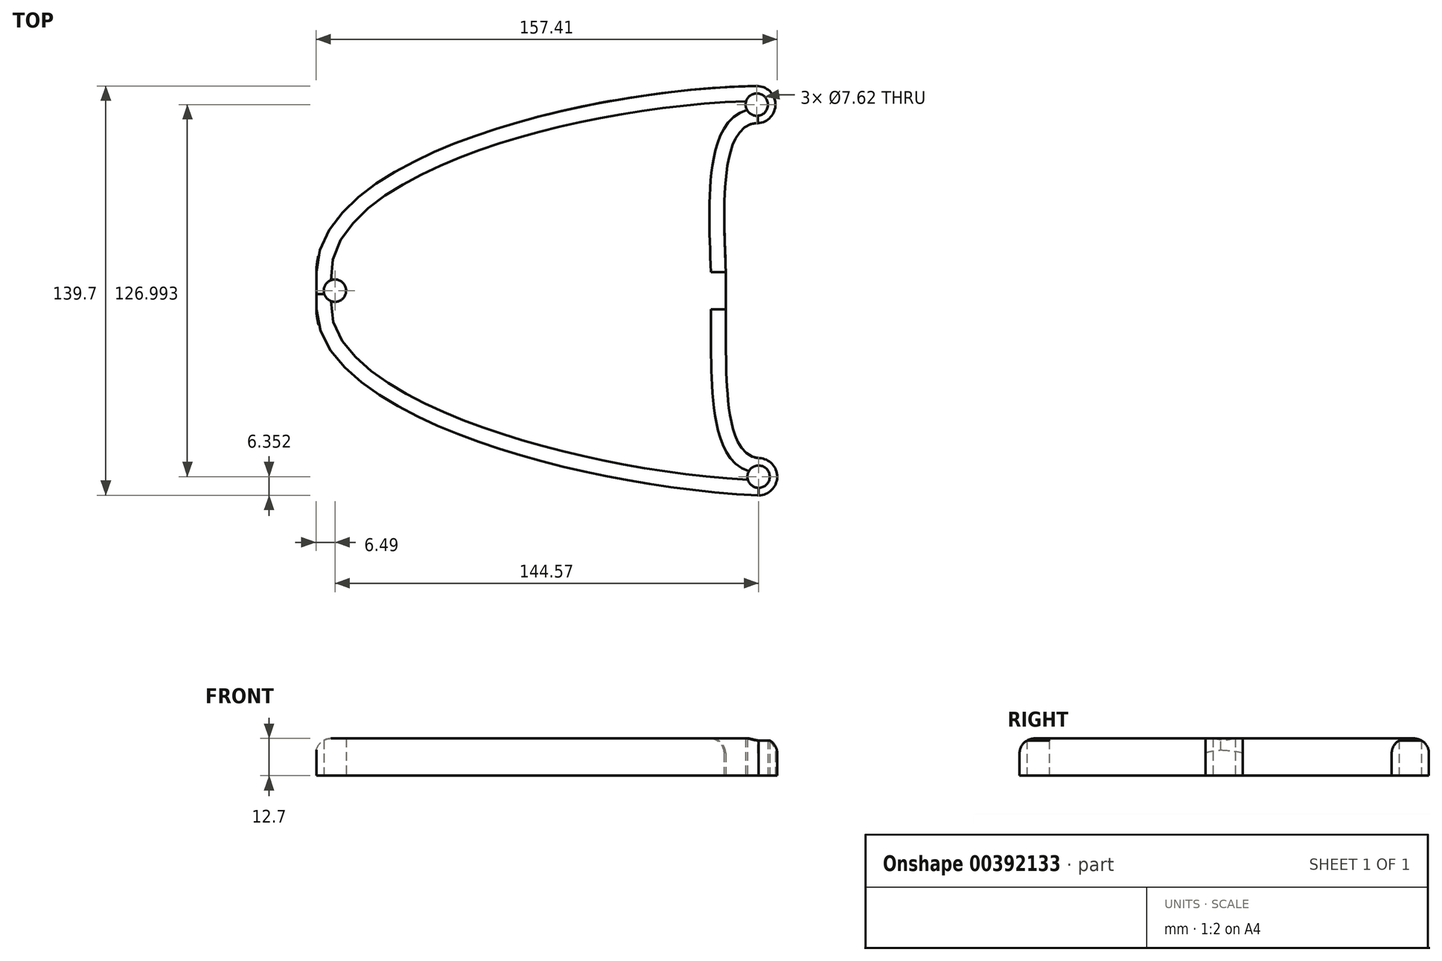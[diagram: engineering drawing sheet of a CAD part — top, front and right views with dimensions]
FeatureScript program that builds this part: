
annotation { "Feature Type Name" : "Feature", "Feature Type Description" : "" }
export const myFeature = defineFeature(function(context is Context, id is Id, definition is map)
    precondition{}
    {
        {
            var Q0;
            Q0=qCreatedBy(makeId("Top.planeOp"),FACE);
            var sketch = newSketch(context, id + "F0", { "sketchPlane" : qUnion([Q0])});
            skLineSegment(sketch, "E0.bottom", {"start": v(69.85, 6.35) * mm, "end": v(-69.85, 6.35) * mm});
            skLineSegment(sketch, "E0.top", {"start": v(69.85, -6.35) * mm, "end": v(-69.85, -6.35) * mm});
            skLineSegment(sketch, "E0.left", {"start": v(69.85, 6.35) * mm, "end": v(69.85, -6.35) * mm});
            skLineSegment(sketch, "E0.right", {"start": v(-69.85, 6.35) * mm, "end": v(-69.85, -6.35) * mm});
            skPoint(sketch, "E0.middle", {"position": v(0, 0) * mm});
            skFitSpline(sketch, "E1", {"points": [v(-69.85, -6.35) * mm, v(81.07, -69.85) * mm], "startDerivative": vector(2.9, -111.28) * mm, "endDerivative": vector(173.62, -7.2) * mm});
            skFitSpline(sketch, "E2", {"points": [v(69.85, -6.35) * mm, v(81.3, -57.15) * mm], "startDerivative": vector(0.84, -63.74) * mm, "endDerivative": vector(38.18, -1.44) * mm});
            skArc(sketch, "E3", {"start": v(81.3, -57.15) * mm, "mid": v(87.42, -63.62) * mm, "end": v(81.07, -69.85) * mm});
            skCircle(sketch, "E4", {"center": v(81.07, -63.5) * mm, "radius": 3.81 * mm});
            skFitSpline(sketch, "E5", {"points": [v(69.85, 6.35) * mm, v(80.83, 57.15) * mm], "startDerivative": vector(-0.6, 42.25) * mm, "endDerivative": vector(43.95, -0.79) * mm});
            skFitSpline(sketch, "E6", {"points": [v(-69.85, 6.35) * mm, v(80.35, 69.85) * mm], "startDerivative": vector(2.18, 120.77) * mm, "endDerivative": vector(169.3, 2.88) * mm});
            skArc(sketch, "E7", {"start": v(80.35, 69.85) * mm, "mid": v(86.8, 63.74) * mm, "end": v(80.83, 57.15) * mm});
            skCircle(sketch, "E8", {"center": v(80.46, 63.5) * mm, "radius": 3.81 * mm});
            skCircle(sketch, "E9", {"center": v(-63.5, 0) * mm, "radius": 3.81 * mm});
            skPoint(sketch, "E9.centerSnap0", {"position": v(-69.85, 0) * mm});
            skSolve(sketch);
        }
        {
            var Q0;
            Q0=makeQuery(id+"F0.imprint","IMPRINT",FACE,{"disambiguationData":[TD([[makeQuery(id+"F0.imprint","IMPRINT",EDGE,{"derivedFrom":sQuery(id+"F0.wireOp",EDGE,"E0.bottom")}),-1.0]])]});
            var Q1;
            Q1=makeQuery(id+"F0.imprint","IMPRINT",FACE,{"disambiguationData":[TD([[makeQuery(id+"F0.imprint","IMPRINT",EDGE,{"derivedFrom":sQuery(id+"F0.wireOp",EDGE,"E0.bottom")}),1.0]])]});
            var Q2;
            Q2=makeQuery(id+"F0.imprint","IMPRINT",FACE,{"disambiguationData":[TD([[makeQuery(id+"F0.imprint","IMPRINT",EDGE,{"derivedFrom":sQuery(id+"F0.wireOp",EDGE,"E0.top")}),1.0]])]});
            extrude(context, id + "F1", {"entities" : qUnion([Q0, Q1, Q2]), "depth" : 12.7 * mm});
        }
        {
            var Q0;
            Q0=makeQuery(id+"F1.opExtrude","CAP_EDGE",EDGE,{"disambiguationData":[OSD([sQuery(id+"F0.wireOp",EDGE,"E1")])],"isStart":false});
            var Q1;
            Q1=makeQuery(id+"F1.opExtrude","CAP_EDGE",EDGE,{"disambiguationData":[OSD([sQuery(id+"F0.wireOp",EDGE,"E6")])],"isStart":false});
            var Q2;
            Q2=makeQuery(id+"F1.opExtrude","CAP_EDGE",EDGE,{"disambiguationData":[OSD([sQuery(id+"F0.wireOp",EDGE,"E2")])],"isStart":false});
            var Q3;
            Q3=makeQuery(id+"F1.opExtrude","CAP_EDGE",EDGE,{"disambiguationData":[OSD([sQuery(id+"F0.wireOp",EDGE,"E5")])],"isStart":false});
            var Q4;
            Q4=makeQuery(id+"F1.opExtrude","CAP_EDGE",EDGE,{"disambiguationData":[OSD([sQuery(id+"F0.wireOp",EDGE,"E0.left")])],"isStart":false});
            var Q5;
            Q5=makeQuery(id+"F1.opExtrude","CAP_EDGE",EDGE,{"disambiguationData":[OSD([sQuery(id+"F0.wireOp",EDGE,"E7")])],"isStart":false});
            var Q6;
            Q6=makeQuery(id+"F1.opExtrude","CAP_EDGE",EDGE,{"disambiguationData":[OSD([sQuery(id+"F0.wireOp",EDGE,"E3")])],"isStart":false});
            fillet(context, id + "F2", {"entities" : qUnion([Q0, Q1, Q2, Q3, Q4, Q5, Q6]), "radius" : 5.08 * mm, "tangentPropagation" : true, "allowEdgeOverflow" : false});
        }
    });
